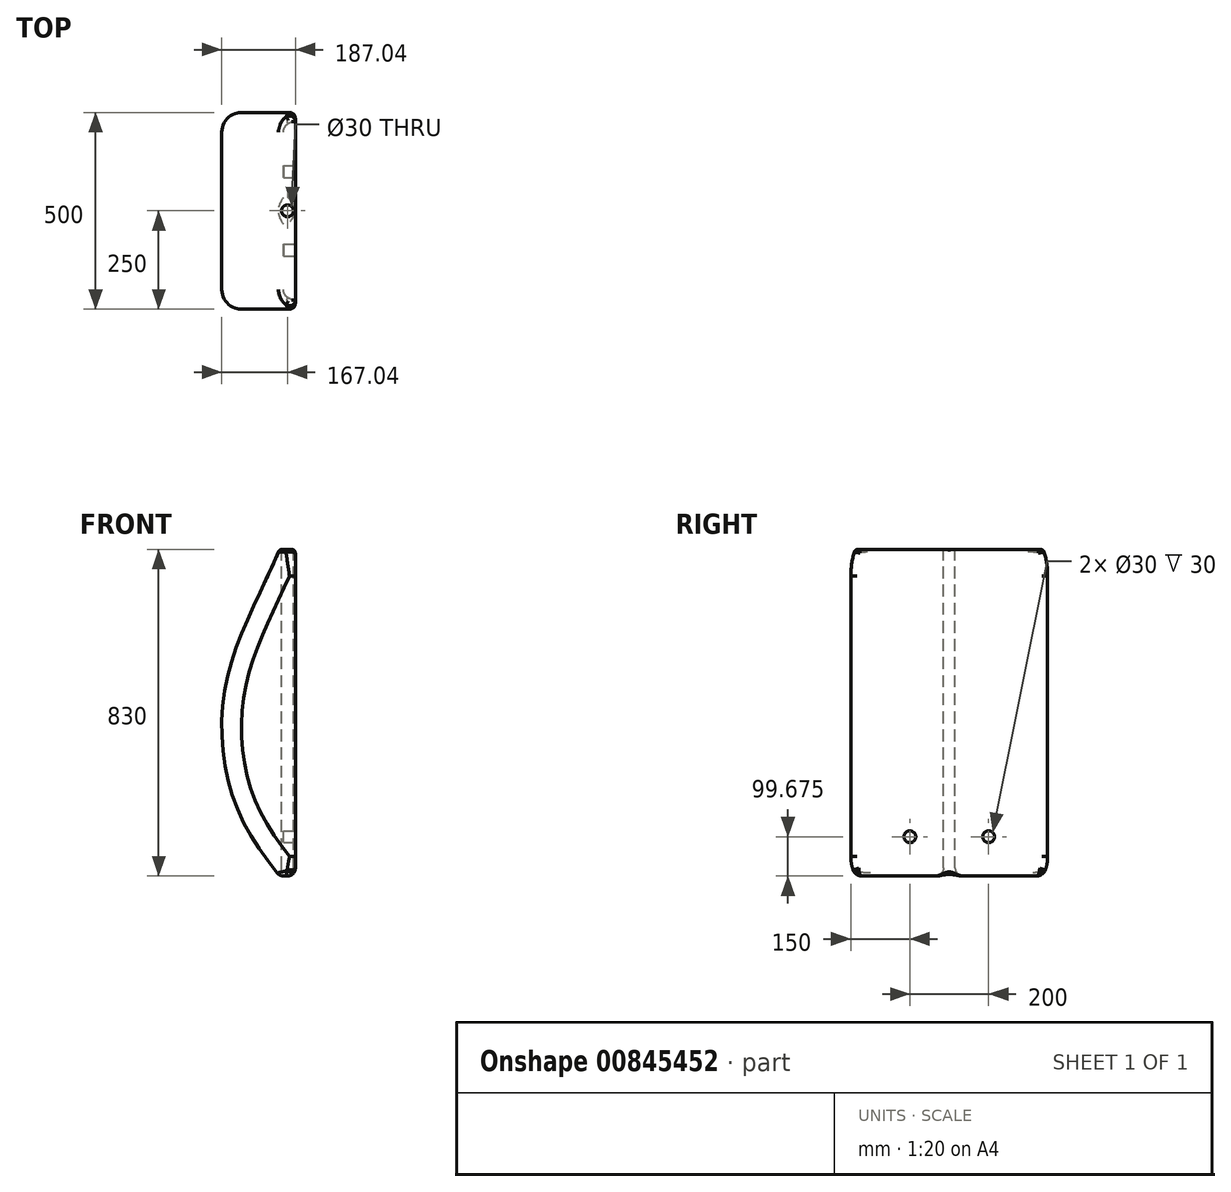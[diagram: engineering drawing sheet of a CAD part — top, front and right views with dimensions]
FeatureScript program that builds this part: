
annotation { "Feature Type Name" : "Feature", "Feature Type Description" : "" }
export const myFeature = defineFeature(function(context is Context, id is Id, definition is map)
    precondition{}
    {
        {
            var Q0;
            Q0=qCreatedBy(makeId("Front.planeOp"),FACE);
            var sketch = newSketch(context, id + "F0", { "sketchPlane" : qUnion([Q0])});
            skFitSpline(sketch, "E0", {"points": [v(-40, 830) * mm, v(-175.73, 490.7) * mm, v(-151.68, 181.43) * mm, v(-40, 0) * mm], "startDerivative": vector(-357.78, -854.6) * mm, "endDerivative": vector(442.11, -563.9) * mm});
            skLineSegment(sketch, "E1", {"start": v(-40, 830) * mm, "end": v(118.07, 830) * mm});
            skLineSegment(sketch, "E2", {"start": v(-82.95, 0) * mm, "end": v(112.91, 0) * mm});
            skLineSegment(sketch, "E3", {"start": v(0, 886.1) * mm, "end": v(0, -37.96) * mm});
            skSolve(sketch);
        }
        {
            var Q0;
            {var subQ0=sQuery(id+"F0.wireOp",EDGE,"E0");Q0=makeQuery(id+"F0.imprint","IMPRINT",FACE,{"disambiguationData":[TD([[makeQuery(id+"F0.imprint","IMPRINT",EDGE,{"derivedFrom":subQ0}),1.0]])]});}
            extrude(context, id + "F1", {"entities" : qUnion([Q0]), "depth" : 500 * mm, "offsetDistance" : 25 * mm});
        }
        {
            var Q0;
            Q0=makeQuery(id+"F1.opExtrude","SWEPT_FACE",FACE,{"disambiguationData":[OSD([sQuery(id+"F0.wireOp",EDGE,"E1")])]});
            var sketch = newSketch(context, id + "F2", { "sketchPlane" : qUnion([Q0])});
            skPoint(sketch, "E4.centerSnap0", {"position": v(-40, -250) * mm});
            skCircle(sketch, "E5", {"center": v(-20, -250) * mm, "radius": 15 * mm});
            skSolve(sketch);
        }
        {
            var Q0;
            Q0=makeQuery(id+"F2.imprint","IMPRINT",FACE,{"disambiguationData":[TD([[makeQuery(id+"F2.imprint","IMPRINT",EDGE,{"derivedFrom":sQuery(id+"F2.wireOp",EDGE,"E5")}),1.0]])]});
            extrude(context, id + "F3", {"entities" : qUnion([Q0]), "operationType" : NewBodyOperationType.REMOVE, "endBound" : BoundingType.UP_TO_NEXT, "oppositeDirection" : true, "depth" : 25 * mm, "offsetDistance" : 25 * mm});
        }
        {
            var Q0;
            Q0=makeQuery(id+"F1.opExtrude","CAP_EDGE",EDGE,{"disambiguationData":[OSD([sQuery(id+"F0.wireOp",EDGE,"E0")])],"isStart":false});
            var Q1;
            Q1=makeQuery(id+"F1.opExtrude","CAP_EDGE",EDGE,{"disambiguationData":[OSD([sQuery(id+"F0.wireOp",EDGE,"E0")])],"isStart":true});
            fillet(context, id + "F4", {"entities" : qUnion([Q0, Q1]), "radius" : 50 * mm, "tangentPropagation" : true, "allowEdgeOverflow" : false});
        }
        {
            var Q0;
            Q0=makeQuery(id+"F1.opExtrude","SWEPT_EDGE",EDGE,{"disambiguationData":[OSD([sQuery(id+"F0.wireOp",EDGE,"E1"),sQuery(id+"F0.wireOp",EDGE,"E3")])]});
            var Q1;
            Q1=makeQuery(id+"F1.opExtrude","SWEPT_EDGE",EDGE,{"disambiguationData":[OSD([sQuery(id+"F0.wireOp",EDGE,"E0"),sQuery(id+"F0.wireOp",EDGE,"E1")])]});
            fillet(context, id + "F5", {"entities" : qUnion([Q0, Q1]), "radius" : 10 * mm, "tangentPropagation" : true, "allowEdgeOverflow" : false});
        }
        {
            var Q0;
            Q0=makeQuery(id+"F1.opExtrude","CAP_EDGE",EDGE,{"disambiguationData":[OSD([sQuery(id+"F0.wireOp",EDGE,"E3")])],"isStart":false});
            var Q1;
            Q1=makeQuery(id+"F1.opExtrude","CAP_EDGE",EDGE,{"disambiguationData":[OSD([sQuery(id+"F0.wireOp",EDGE,"E3")])],"isStart":true});
            fillet(context, id + "F6", {"entities" : qUnion([Q0, Q1]), "radius" : 15 * mm, "tangentPropagation" : true, "allowEdgeOverflow" : false});
        }
        {
            var Q0;
            Q0=makeQuery(id+"F6.opFillet","BLEND_EDGE",EDGE,{"blendedFrom":[makeQuery(id+"F4.opFillet","BLEND_EDGE",EDGE,{"disambiguationData":[OD(1.0)],"blendedFrom":[makeQuery(id+"F1.opExtrude","CAP_EDGE",EDGE,{"disambiguationData":[OSD([sQuery(id+"F0.wireOp",EDGE,"E0")])],"isStart":false}),makeQuery(id+"F1.opExtrude","SWEPT_FACE",FACE,{"disambiguationData":[OSD([sQuery(id+"F0.wireOp",EDGE,"E3")])]})],"blendedInto":[makeQuery(id+"F1.opExtrude","SWEPT_FACE",FACE,{"disambiguationData":[OSD([sQuery(id+"F0.wireOp",EDGE,"E3")])]})]}),makeQuery(id+"F1.opExtrude","SWEPT_FACE",FACE,{"disambiguationData":[OSD([sQuery(id+"F0.wireOp",EDGE,"E2")])]})],"blendedInto":[makeQuery(id+"F1.opExtrude","SWEPT_FACE",FACE,{"disambiguationData":[OSD([sQuery(id+"F0.wireOp",EDGE,"E2")])]})]});
            var Q1;
            Q1=makeQuery(id+"F1.opExtrude","SWEPT_FACE",FACE,{"disambiguationData":[OSD([sQuery(id+"F0.wireOp",EDGE,"E2")])]});
            fillet(context, id + "F7", {"entities" : qUnion([Q0, Q1]), "radius" : 20 * mm, "tangentPropagation" : true, "allowEdgeOverflow" : false});
        }
        {
            var Q0;
            Q0=makeQuery(id+"F1.opExtrude","SWEPT_FACE",FACE,{"disambiguationData":[OSD([sQuery(id+"F0.wireOp",EDGE,"E3")])]});
            var sketch = newSketch(context, id + "F8", { "sketchPlane" : qUnion([Q0])});
            skCircle(sketch, "E6", {"center": v(-350, 99.68) * mm, "radius": 15 * mm});
            skCircle(sketch, "E7", {"center": v(-150, 99.68) * mm, "radius": 15 * mm});
            skSolve(sketch);
        }
        {
            var Q0;
            Q0=makeQuery(id+"F8.imprint","IMPRINT",FACE,{"disambiguationData":[TD([[makeQuery(id+"F8.imprint","IMPRINT",EDGE,{"derivedFrom":sQuery(id+"F8.wireOp",EDGE,"E6")}),1.0]])]});
            var Q1;
            Q1=makeQuery(id+"F8.imprint","IMPRINT",FACE,{"disambiguationData":[TD([[makeQuery(id+"F8.imprint","IMPRINT",EDGE,{"derivedFrom":sQuery(id+"F8.wireOp",EDGE,"E7")}),1.0]])]});
            extrude(context, id + "F9", {"entities" : qUnion([Q0, Q1]), "operationType" : NewBodyOperationType.REMOVE, "oppositeDirection" : true, "depth" : 30 * mm, "offsetDistance" : 25 * mm});
        }
    });
